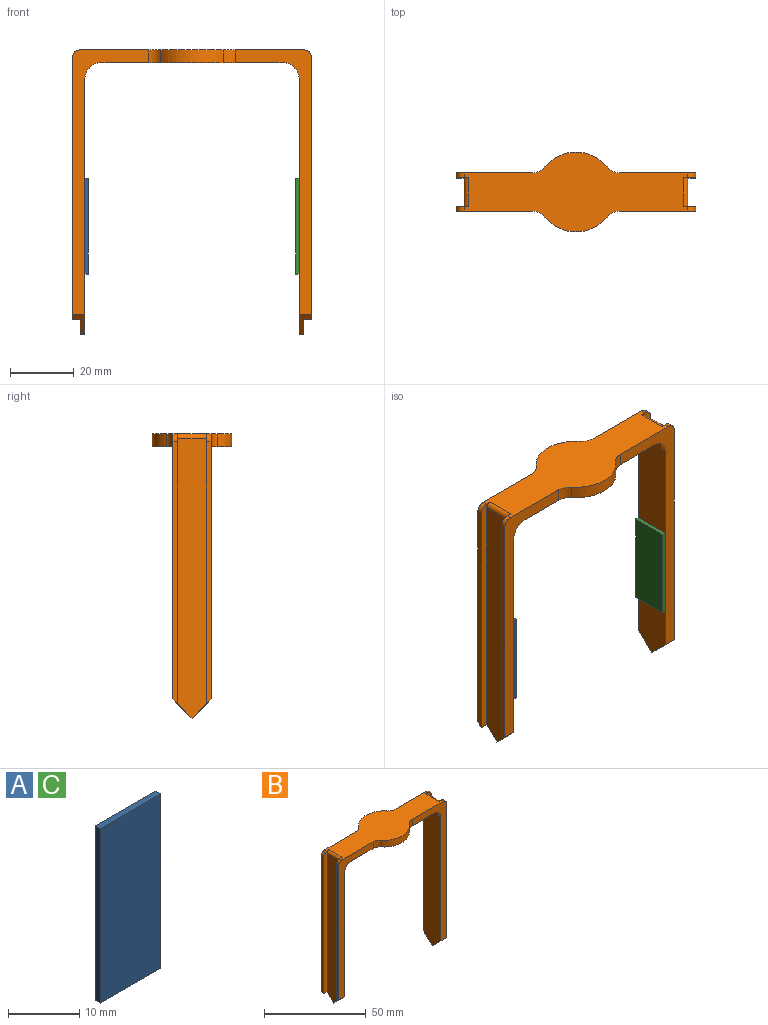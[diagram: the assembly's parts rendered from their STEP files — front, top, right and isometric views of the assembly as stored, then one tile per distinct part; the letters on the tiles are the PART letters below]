
ASSEMBLY  parts=3 mates=2
PART A: 6 faces, bbox 12x1x30 mm
  f0: plane 12x1mm, normal (0,0,1), area 12mm2, adj f1,f3,f4,f5
  f1: plane 30x1mm, normal (-1,0,0), area 30mm2, adj f0,f2,f4,f5
  f2: plane 12x1mm, normal (0,0,-1), area 12mm2, adj f1,f3,f4,f5
  f3: plane 30x1mm, normal (1,0,0), area 30mm2, adj f0,f2,f4,f5
  f4: plane 30x12mm, normal (0,-1,0), area 360mm2, adj f0,f1,f2,f3
  f5: plane 30x12mm, normal (0,1,0), area 360mm2, adj f0,f1,f2,f3
PART B: 48 faces, bbox 75x25x89 mm
  f0: plane 57x8mm, normal (0,0,-1), area 94.9mm2, adj f5,f6,f7,f28,f29,f30,f40,f41
  f1: plane 82x1.5mm, normal (-1,0,0), area 121.9mm2, adj f9,f19,f22,f37
  f2: plane 82x1.5mm, normal (1,0,0), area 121.9mm2, adj f11,f17,f23,f36
  f3: plane 70x25mm, normal (0,0,1), area 1019.7mm2, adj f5,f6,f7,f9,f10,f11,f15,f17
  f4: plane 57x8mm, normal (0,0,-1), area 94.9mm2, adj f9,f10,f11,f25,f26,f27,f42,f43
  f5: plane 83x23.89mm, normal (0,1,0), area 415.6mm2, adj f0,f3,f12,f14,f24,f39,f40,f45
  f6: cylinder r=12.5mm len=19.44mm, axis (0,0,-1), area 89.1mm2, adj f0,f3,f40,f41
  f7: plane 83x23.89mm, normal (0,1,0), area 415.6mm2, adj f0,f3,f8,f13,f21,f38,f41,f44
  f8: plane 82x1.5mm, normal (-1,0,0), area 121.9mm2, adj f7,f18,f21,f38
  f9: plane 83x23.89mm, normal (0,-1,0), area 415.6mm2, adj f1,f3,f4,f13,f22,f37,f42,f47
  f10: cylinder r=12.5mm len=19.44mm, axis (0,0,-1), area 89.1mm2, adj f3,f4,f42,f43
  f11: plane 83x23.89mm, normal (0,-1,0), area 415.6mm2, adj f2,f3,f4,f14,f23,f36,f43,f46
  f12: plane 82x1.5mm, normal (1,0,0), area 121.9mm2, adj f5,f15,f24,f39
  f13: plane 86x12mm, normal (1,0,0), area 978mm2, adj f7,f9,f21,f22,f27,f28,f32,f44
  f14: plane 86x12mm, normal (-1,0,0), area 978mm2, adj f5,f11,f23,f24,f25,f30,f33,f45
  f15: plane 84.5x4mm, normal (0,-1,0), area 210.4mm2, adj f3,f12,f16,f24,f35,f39
  f16: plane 87.5x9mm, normal (1,0,0), area 767.2mm2, adj f15,f17,f23,f24,f35
  f17: plane 84.5x4mm, normal (0,1,0), area 210.4mm2, adj f2,f3,f16,f23,f35,f36
  f18: plane 84.5x4mm, normal (0,-1,0), area 210.4mm2, adj f3,f8,f20,f21,f34,f38
  f19: plane 84.5x4mm, normal (0,1,0), area 210.4mm2, adj f1,f3,f20,f22,f34,f37
  f20: plane 87.5x9mm, normal (-1,0,0), area 767.2mm2, adj f18,f19,f21,f22,f34
  f21: plane 6x6mm, normal (0,0.71,-0.71), area 18mm2, adj f7,f8,f13,f18,f20,f22
  f22: plane 6x6mm, normal (0,-0.71,-0.71), area 18mm2, adj f1,f9,f13,f19,f20,f21
  f23: plane 6x6mm, normal (0,-0.71,-0.71), area 18mm2, adj f2,f11,f14,f16,f17,f24
  f24: plane 6x6mm, normal (0,0.71,-0.71), area 18mm2, adj f5,f12,f14,f15,f16,f23
  f25: plane 23.46x7.5mm, normal (0,1,0), area 63.5mm2, adj f4,f14,f26,f31,f33,f46
  f26: cylinder r=11mm len=20.08mm, axis (0,0,-1), area 63.2mm2, adj f4,f25,f27,f31
  f27: plane 23.46x7.5mm, normal (0,1,0), area 63.5mm2, adj f4,f13,f26,f31,f32,f47
  f28: plane 23.46x7.5mm, normal (0,-1,0), area 63.5mm2, adj f0,f13,f29,f31,f32,f44
  f29: cylinder r=11mm len=20.08mm, axis (0,0,-1), area 63.2mm2, adj f0,f28,f30,f31
  f30: plane 23.46x7.5mm, normal (0,-1,0), area 63.5mm2, adj f0,f14,f29,f31,f33,f45
  f31: plane 64x22mm, normal (0,0,-1), area 763.8mm2, adj f25,f26,f27,f28,f29,f30,f32,f33
  f32: cylinder r=1.5mm len=9mm, axis (0,-1,0), area 21.2mm2, adj f13,f27,f28,f31
  f33: cylinder r=1.5mm len=9mm, axis (0,1,0), area 21.2mm2, adj f14,f25,f30,f31
  f34: cylinder r=1.5mm len=9mm, axis (0,-1,0), area 21.2mm2, adj f3,f18,f19,f20
  f35: cylinder r=1.5mm len=9mm, axis (0,1,0), area 21.2mm2, adj f3,f15,f16,f17
  f36: cylinder r=2.5mm len=2.5mm, axis (0,-1,0), area 5.9mm2, adj f2,f3,f11,f17
  f37: cylinder r=2.5mm len=2.5mm, axis (0,1,0), area 5.9mm2, adj f1,f3,f9,f19
  f38: cylinder r=2.5mm len=2.5mm, axis (0,1,0), area 5.9mm2, adj f3,f7,f8,f18
  f39: cylinder r=2.5mm len=2.5mm, axis (0,-1,0), area 5.9mm2, adj f3,f5,f12,f15
  f40: cylinder r=5mm len=4mm, axis (0,0,-1), area 17.8mm2, adj f0,f3,f5,f6
  f41: cylinder r=5mm len=4mm, axis (0,0,-1), area 17.8mm2, adj f0,f3,f6,f7
  f42: cylinder r=5mm len=4mm, axis (0,0,-1), area 17.8mm2, adj f3,f4,f9,f10
  f43: cylinder r=5mm len=4mm, axis (0,0,-1), area 17.8mm2, adj f3,f4,f10,f11
  f44: cylinder r=5mm len=5mm, axis (0,1,0), area 11.8mm2, adj f0,f7,f13,f28
  f45: cylinder r=5mm len=5mm, axis (0,-1,0), area 11.8mm2, adj f0,f5,f14,f30
  f46: cylinder r=5mm len=5mm, axis (0,-1,0), area 11.8mm2, adj f4,f11,f14,f25
  f47: cylinder r=5mm len=5mm, axis (0,1,0), area 11.8mm2, adj f4,f9,f13,f27
PART C: same geometry as A
PLACE A rot(axis=(0,0,1),90deg) t=(-33.5,-6,-70.23)mm
PLACE B t=(0,0,-4)mm
PLACE C rot(axis=(0.71,0.71,0),180deg) t=(33.5,-6,-40.23)mm
MATE fastened C.f5 <-> B.f14  axis (1,0,0) through (33.5,0,-55.23)mm
MATE fastened A.f5 <-> B.f13  axis (-1,0,0) through (-33.5,0,-55.23)mm
